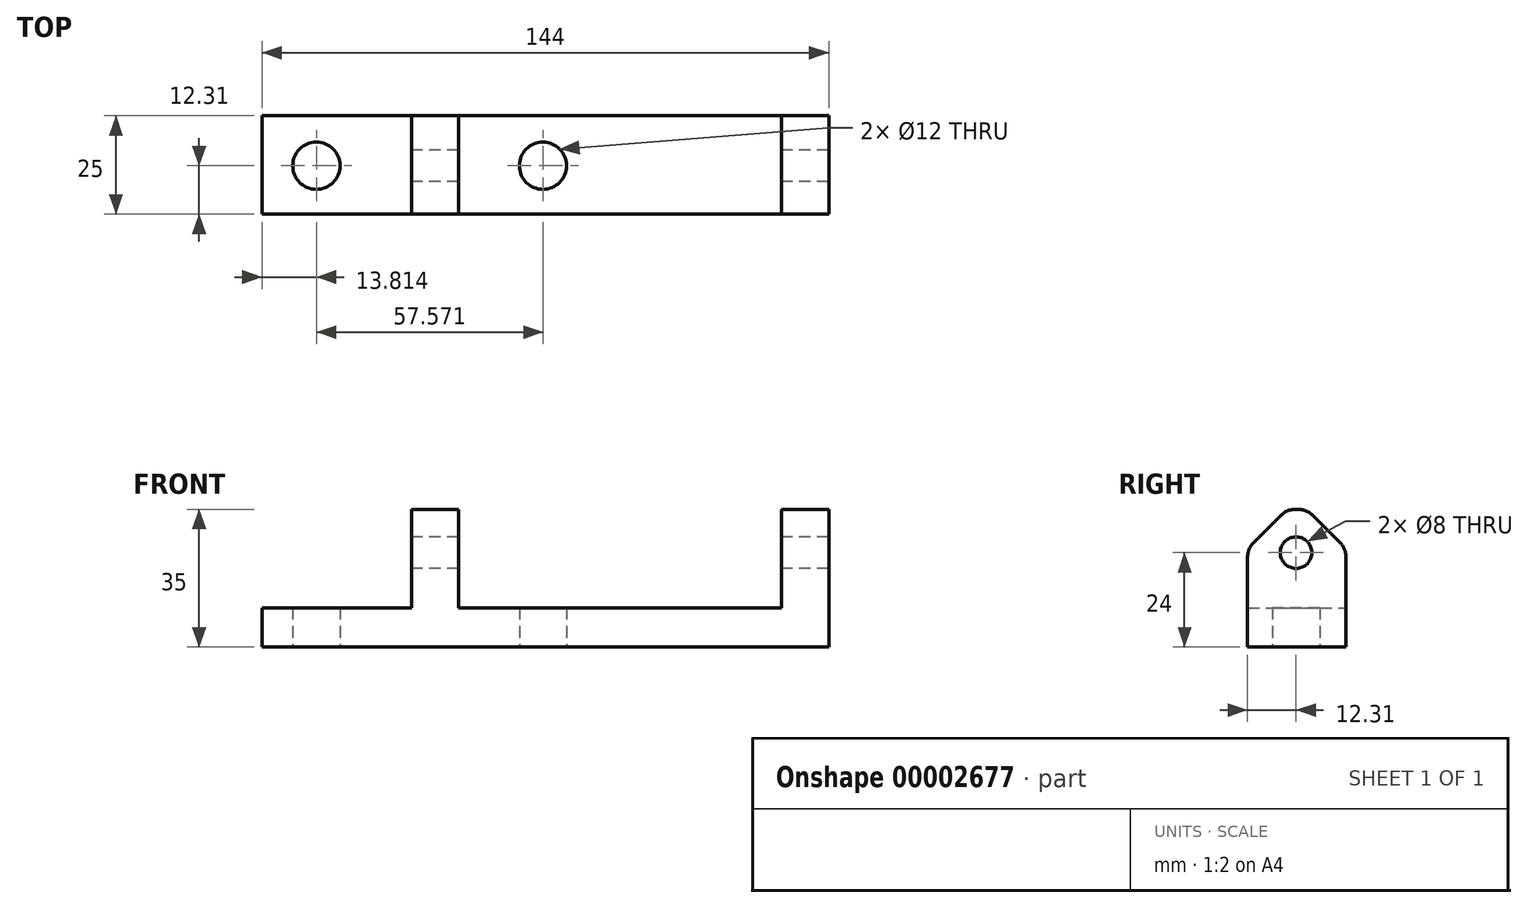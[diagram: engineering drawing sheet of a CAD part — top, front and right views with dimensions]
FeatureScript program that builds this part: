
annotation { "Feature Type Name" : "Feature", "Feature Type Description" : "" }
export const myFeature = defineFeature(function(context is Context, id is Id, definition is map)
    precondition{}
    {
        {
            var Q0;
            Q0=qCreatedBy(makeId("Top.planeOp"),FACE);
            var sketch = newSketch(context, id + "F0", { "sketchPlane" : qUnion([Q0])});
            skLineSegment(sketch, "E0", {"start": v(96.98, -12.31) * mm, "end": v(96.98, 12.69) * mm});
            skLineSegment(sketch, "E1", {"start": v(96.98, 12.69) * mm, "end": v(-47.02, 12.69) * mm});
            skLineSegment(sketch, "E2", {"start": v(-47.02, 12.69) * mm, "end": v(-47.02, -12.31) * mm});
            skLineSegment(sketch, "E3", {"start": v(-47.02, -12.31) * mm, "end": v(96.98, -12.31) * mm});
            skLineSegment(sketch, "E4", {"start": v(-32.39, -5.94) * mm, "end": v(-32.39, -5.92) * mm});
            skLineSegment(sketch, "E5", {"start": v(-39.2, 0) * mm, "end": v(-39.12, 0) * mm});
            skCircle(sketch, "E6", {"center": v(-33.2, 0) * mm, "radius": 6 * mm});
            skPoint(sketch, "E7.orphan", {"position": v(-47.02, 0) * mm});
            skCircle(sketch, "E8", {"center": v(24.36, 0) * mm, "radius": 6 * mm});
            skSolve(sketch);
        }
        {
            var Q0;
            Q0 = qSketchRegion(id + "F0", true);
            extrude(context, id + "F1", {"entities" : qUnion([Q0]), "depth" : 15 * mm});
        }
        {
            var Q0;
            Q0=makeQuery(id+"F1.opExtrude","CAP_FACE",FACE,{"disambiguationData":[OSD([sQuery(id+"F0.wireOp",EDGE,"E0"),sQuery(id+"F0.wireOp",EDGE,"E1"),sQuery(id+"F0.wireOp",EDGE,"E2"),sQuery(id+"F0.wireOp",EDGE,"E3"),sQuery(id+"F0.wireOp",EDGE,"E6"),sQuery(id+"F0.wireOp",EDGE,"E8")])],"isStart":false});
            var sketch = newSketch(context, id + "F2", { "sketchPlane" : qUnion([Q0])});
            skLineSegment(sketch, "E9", {"start": v(84.98, -12.31) * mm, "end": v(84.98, 12.69) * mm});
            skPoint(sketch, "E10.end.orphan", {"position": v(84.98, 0) * mm});
            skPoint(sketch, "E10.start.orphan", {"position": v(96.98, 0) * mm});
            skLineSegment(sketch, "E11", {"start": v(2.98, -12.31) * mm, "end": v(2.98, 12.69) * mm});
            skLineSegment(sketch, "E12", {"start": v(-9.02, -12.31) * mm, "end": v(-9.02, 12.69) * mm});
            skPoint(sketch, "E13.end.orphan", {"position": v(-9.02, 0) * mm});
            skPoint(sketch, "E14.end.orphan", {"position": v(2.98, 0) * mm});
            skSolve(sketch);
        }
        {
            var Q0;
            {var subQ2=sQuery(id+"F2.wireOp",EDGE,"E11");Q0=makeQuery(id+"F2.imprint","IMPRINT",FACE,{"disambiguationData":[TD([[makeQuery(id+"F2.imprint","IMPRINT",EDGE,{"derivedFrom":subQ2}),1.0]])]});}
            var Q1;
            {var subQ1=sQuery(id+"F2.wireOp",EDGE,"E9");Q1=makeQuery(id+"F2.imprint","IMPRINT",FACE,{"disambiguationData":[TD([[makeQuery(id+"F2.imprint","IMPRINT",EDGE,{"derivedFrom":subQ1}),-1.0]])]});}
            extrude(context, id + "F3", {"entities" : qUnion([Q0, Q1]), "operationType" : NewBodyOperationType.ADD, "depth" : 25 * mm});
        }
        {
            var Q0;
            Q0=makeQuery(id+"F3.opExtrude","SWEPT_FACE",FACE,{"disambiguationData":[OSD([sQuery(id+"F2.wireOp",EDGE,"E9")])]});
            var sketch = newSketch(context, id + "F4", { "sketchPlane" : qUnion([Q0])});
            skCircle(sketch, "E15", {"center": v(0, 29) * mm, "radius": 4 * mm});
            skPoint(sketch, "E16.start.orphan", {"position": v(0, 15) * mm});
            skSolve(sketch);
        }
        {
            var Q0;
            Q0=makeQuery(id+"F4.imprint","IMPRINT",FACE,{"disambiguationData":[TD([[makeQuery(id+"F4.imprint","IMPRINT",EDGE,{"derivedFrom":sQuery(id+"F4.wireOp",EDGE,"E15")}),1.0]])]});
            var Q1;
            {var subQ0=sQuery(id+"F0.wireOp",EDGE,"E0");Q1=makeQuery(id+"F3.boolean.opBoolean","MERGE",FACE,{"derivedFrom":[makeQuery(id+"F1.opExtrude","SWEPT_FACE",FACE,{"disambiguationData":[OSD([subQ0])]}),makeQuery(id+"F3.opExtrude","SWEPT_FACE",FACE,{"disambiguationData":[OSD([subQ0])]})]});}
            extrude(context, id + "F5", {"entities" : qUnion([Q0]), "operationType" : NewBodyOperationType.REMOVE, "endBound" : BoundingType.UP_TO_SURFACE, "oppositeDirection" : true, "endBoundEntityFace" : qUnion([Q1]), "depth" : 25 * mm});
        }
        {
            var Q0;
            Q0=makeQuery(id+"F3.opExtrude","CAP_EDGE",EDGE,{"disambiguationData":[OSD([sQuery(id+"F0.wireOp",EDGE,"E3")])],"isStart":false});
            var Q1;
            Q1=makeQuery(id+"F3.opExtrude","CAP_EDGE",EDGE,{"disambiguationData":[OSD([sQuery(id+"F0.wireOp",EDGE,"E1")])],"isStart":false});
            chamfer(context, id + "F6", {"entities" : qUnion([Q0, Q1]), "width" : 10 * mm, "tangentPropagation" : true});
        }
        {
            var Q0;
            {var subQ0=sQuery(id+"F0.wireOp",EDGE,"E1");Q0=makeQuery(id+"F6.opChamfer","BLEND_EDGE",EDGE,{"blendedFrom":[makeQuery(id+"F3.opExtrude","CAP_EDGE",EDGE,{"disambiguationData":[OSD([subQ0])],"isStart":false}),makeQuery(id+"F3.opExtrude","CAP_FACE",FACE,{"disambiguationData":[OSD([sQuery(id+"F0.wireOp",EDGE,"E0"),subQ0,sQuery(id+"F0.wireOp",EDGE,"E3"),sQuery(id+"F2.wireOp",EDGE,"E9")])],"isStart":false})],"blendedInto":[makeQuery(id+"F3.opExtrude","CAP_FACE",FACE,{"disambiguationData":[OSD([sQuery(id+"F0.wireOp",EDGE,"E0"),subQ0,sQuery(id+"F0.wireOp",EDGE,"E3"),sQuery(id+"F2.wireOp",EDGE,"E9")])],"isStart":false})]});}
            var Q1;
            {var subQ0=sQuery(id+"F0.wireOp",EDGE,"E1");Q1=makeQuery(id+"F6.opChamfer","BLEND_EDGE",EDGE,{"blendedFrom":[makeQuery(id+"F3.opExtrude","CAP_EDGE",EDGE,{"disambiguationData":[OSD([subQ0])],"isStart":false}),makeQuery(id+"F3.boolean.opBoolean","MERGE",FACE,{"derivedFrom":[makeQuery(id+"F1.opExtrude","SWEPT_FACE",FACE,{"disambiguationData":[OSD([subQ0])]}),makeQuery(id+"F3.opExtrude","SWEPT_FACE",FACE,{"disambiguationData":[OSD([subQ0])]})]})],"blendedInto":[makeQuery(id+"F3.boolean.opBoolean","MERGE",FACE,{"derivedFrom":[makeQuery(id+"F1.opExtrude","SWEPT_FACE",FACE,{"disambiguationData":[OSD([subQ0])]}),makeQuery(id+"F3.opExtrude","SWEPT_FACE",FACE,{"disambiguationData":[OSD([subQ0])]})]})]});}
            var Q2;
            {var subQ0=sQuery(id+"F0.wireOp",EDGE,"E3");Q2=makeQuery(id+"F6.opChamfer","BLEND_EDGE",EDGE,{"blendedFrom":[makeQuery(id+"F3.opExtrude","CAP_EDGE",EDGE,{"disambiguationData":[OSD([subQ0])],"isStart":false}),makeQuery(id+"F3.opExtrude","CAP_FACE",FACE,{"disambiguationData":[OSD([sQuery(id+"F0.wireOp",EDGE,"E0"),sQuery(id+"F0.wireOp",EDGE,"E1"),subQ0,sQuery(id+"F2.wireOp",EDGE,"E9")])],"isStart":false})],"blendedInto":[makeQuery(id+"F3.opExtrude","CAP_FACE",FACE,{"disambiguationData":[OSD([sQuery(id+"F0.wireOp",EDGE,"E0"),sQuery(id+"F0.wireOp",EDGE,"E1"),subQ0,sQuery(id+"F2.wireOp",EDGE,"E9")])],"isStart":false})]});}
            var Q3;
            {var subQ0=sQuery(id+"F0.wireOp",EDGE,"E3");Q3=makeQuery(id+"F6.opChamfer","BLEND_EDGE",EDGE,{"blendedFrom":[makeQuery(id+"F3.opExtrude","CAP_EDGE",EDGE,{"disambiguationData":[OSD([subQ0])],"isStart":false}),makeQuery(id+"F3.boolean.opBoolean","MERGE",FACE,{"derivedFrom":[makeQuery(id+"F1.opExtrude","SWEPT_FACE",FACE,{"disambiguationData":[OSD([subQ0])]}),makeQuery(id+"F3.opExtrude","SWEPT_FACE",FACE,{"disambiguationData":[OSD([subQ0])]})]})],"blendedInto":[makeQuery(id+"F3.boolean.opBoolean","MERGE",FACE,{"derivedFrom":[makeQuery(id+"F1.opExtrude","SWEPT_FACE",FACE,{"disambiguationData":[OSD([subQ0])]}),makeQuery(id+"F3.opExtrude","SWEPT_FACE",FACE,{"disambiguationData":[OSD([subQ0])]})]})]});}
            var Q4;
            {var subQ0=sQuery(id+"F0.wireOp",EDGE,"E3");var subQ1=makeQuery(id+"F1.opExtrude","CAP_EDGE",EDGE,{"disambiguationData":[OSD([subQ0])],"isStart":false});var subQ2=sQuery(id+"F2.wireOp",EDGE,"E12");var subQ3=sQuery(id+"F2.wireOp",EDGE,"E11");Q4=makeQuery(id+"F6.opChamfer","BLEND_EDGE",EDGE,{"blendedFrom":[makeQuery(id+"F3.opExtrude","CAP_EDGE",EDGE,{"disambiguationData":[OSD([subQ0]),TDD([makeQuery(id+"F2.imprint","IMPRINT",EDGE,{"disambiguationData":[TD([[makeQuery(id+"F2.imprint","INTERSECT",VERTEX,{"derivedFrom":[subQ1,subQ3]}),1.0]])],"derivedFrom":subQ1})])],"isStart":false}),makeQuery(id+"F3.opExtrude","CAP_FACE",FACE,{"disambiguationData":[OSD([sQuery(id+"F0.wireOp",EDGE,"E1"),subQ0,subQ3,subQ2])],"isStart":false})],"blendedInto":[makeQuery(id+"F3.opExtrude","CAP_FACE",FACE,{"disambiguationData":[OSD([sQuery(id+"F0.wireOp",EDGE,"E1"),subQ0,subQ3,subQ2])],"isStart":false})]});}
            var Q5;
            {var subQ0=sQuery(id+"F0.wireOp",EDGE,"E1");var subQ1=makeQuery(id+"F1.opExtrude","CAP_EDGE",EDGE,{"disambiguationData":[OSD([subQ0])],"isStart":false});var subQ2=sQuery(id+"F2.wireOp",EDGE,"E12");var subQ3=sQuery(id+"F2.wireOp",EDGE,"E11");Q5=makeQuery(id+"F6.opChamfer","BLEND_EDGE",EDGE,{"blendedFrom":[makeQuery(id+"F3.opExtrude","CAP_EDGE",EDGE,{"disambiguationData":[OSD([subQ0]),TDD([makeQuery(id+"F2.imprint","IMPRINT",EDGE,{"disambiguationData":[TD([[makeQuery(id+"F2.imprint","INTERSECT",VERTEX,{"derivedFrom":[subQ1,subQ3]}),-1.0]])],"derivedFrom":subQ1})])],"isStart":false}),makeQuery(id+"F3.opExtrude","CAP_FACE",FACE,{"disambiguationData":[OSD([subQ0,sQuery(id+"F0.wireOp",EDGE,"E3"),subQ3,subQ2])],"isStart":false})],"blendedInto":[makeQuery(id+"F3.opExtrude","CAP_FACE",FACE,{"disambiguationData":[OSD([subQ0,sQuery(id+"F0.wireOp",EDGE,"E3"),subQ3,subQ2])],"isStart":false})]});}
            fillet(context, id + "F7", {"entities" : qUnion([Q0, Q1, Q2, Q3, Q4, Q5]), "radius" : 5 * mm, "tangentPropagation" : true, "allowEdgeOverflow" : false});
        }
        {
            var Q0;
            Q0=makeQuery(id+"F3.opExtrude","SWEPT_FACE",FACE,{"disambiguationData":[OSD([sQuery(id+"F2.wireOp",EDGE,"E12")])]});
            var sketch = newSketch(context, id + "F8", { "sketchPlane" : qUnion([Q0])});
            skCircle(sketch, "E17", {"center": v(0, 29) * mm, "radius": 4 * mm});
            skPoint(sketch, "E18.start.orphan", {"position": v(0, 15) * mm});
            skSolve(sketch);
        }
        {
            var Q0;
            Q0=makeQuery(id+"F8.imprint","IMPRINT",FACE,{"disambiguationData":[TD([[makeQuery(id+"F8.imprint","IMPRINT",EDGE,{"derivedFrom":sQuery(id+"F8.wireOp",EDGE,"E17")}),1.0]])]});
            extrude(context, id + "F9", {"entities" : qUnion([Q0]), "operationType" : NewBodyOperationType.REMOVE, "oppositeDirection" : true, "depth" : 25 * mm});
        }
        {
            var Q0;
            Q0=makeQuery(id+"F1.opExtrude","CAP_FACE",FACE,{"disambiguationData":[OSD([sQuery(id+"F0.wireOp",EDGE,"E0"),sQuery(id+"F0.wireOp",EDGE,"E1"),sQuery(id+"F0.wireOp",EDGE,"E2"),sQuery(id+"F0.wireOp",EDGE,"E3"),sQuery(id+"F0.wireOp",EDGE,"E6"),sQuery(id+"F0.wireOp",EDGE,"E8")])],"isStart":true});
            extrude(context, id + "F10", {"entities" : qUnion([Q0]), "operationType" : NewBodyOperationType.REMOVE, "oppositeDirection" : true, "depth" : 5 * mm});
        }
    });
